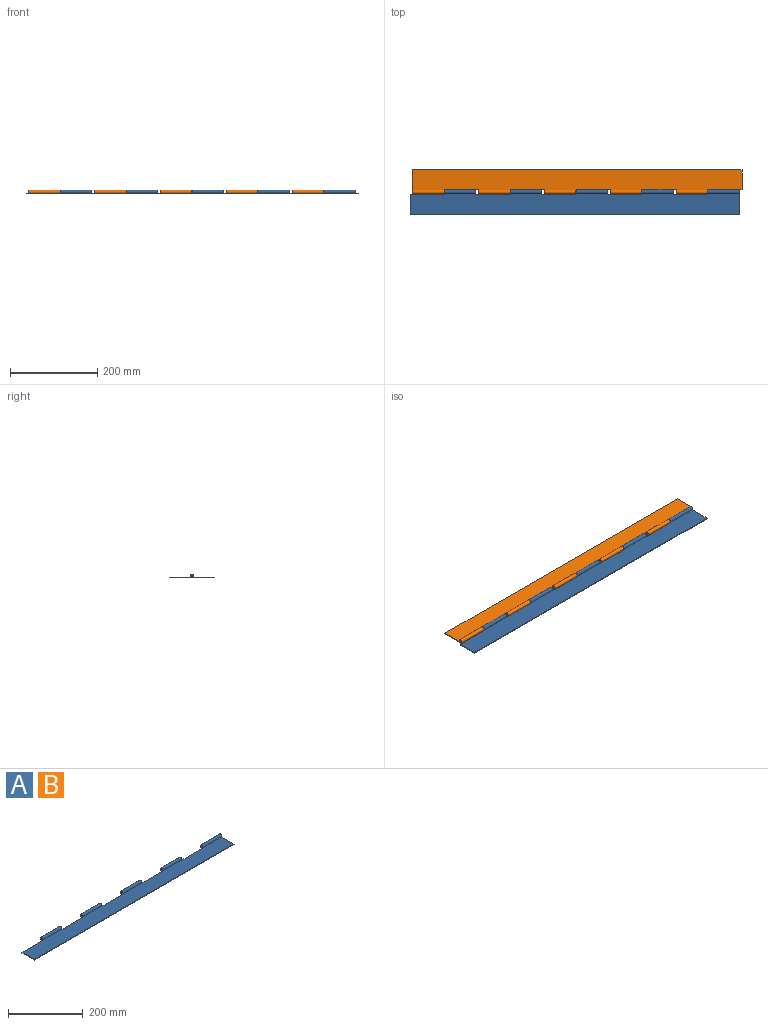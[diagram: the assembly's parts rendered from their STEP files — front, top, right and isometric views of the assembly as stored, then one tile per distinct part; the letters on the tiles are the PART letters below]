
ASSEMBLY  parts=2 mates=1
PART A: 29 faces, bbox 755.7x55.2x8.9 mm
  f0: cylinder r=4.45mm len=72.39mm, axis (-1,0,0), area 1712.7mm2, adj f11,f13,f14,f28
  f1: cylinder r=2.46mm len=72.39mm, axis (-1,0,0), area 1117.3mm2, adj f11,f28
  f2: cylinder r=4.45mm len=72.39mm, axis (-1,0,0), area 1712.7mm2, adj f13,f14,f25,f26
  f3: cylinder r=2.46mm len=72.39mm, axis (-1,0,0), area 1117.3mm2, adj f25,f26
  f4: cylinder r=4.45mm len=72.39mm, axis (-1,0,0), area 1712.7mm2, adj f13,f14,f22,f23
  f5: cylinder r=2.46mm len=72.39mm, axis (-1,0,0), area 1117.3mm2, adj f22,f23
  f6: cylinder r=4.45mm len=72.39mm, axis (-1,0,0), area 1712.7mm2, adj f13,f14,f19,f20
  f7: cylinder r=2.46mm len=72.39mm, axis (-1,0,0), area 1117.3mm2, adj f19,f20
  f8: plane 45.87x1.9mm, normal (-1,0,0), area 87mm2, adj f12,f13,f14,f15
  f9: cylinder r=4.45mm len=72.39mm, axis (-1,0,0), area 1712.7mm2, adj f13,f14,f16,f17
  f10: cylinder r=2.46mm len=72.39mm, axis (-1,0,0), area 1117.3mm2, adj f16,f17
  f11: plane 55.25x8.89mm, normal (1,0,0), area 134.7mm2, adj f0,f1,f12,f13,f14
  f12: plane 755.65x1.9mm, normal (0,-1,0), area 1433.8mm2, adj f8,f11,f13,f14
  f13: plane 755.65x50.8mm, normal (0,0,-1), area 36447.9mm2, adj f0,f2,f4,f6,f8,f9,f11,f12
  f14: plane 755.65x47.16mm, normal (0,0,1), area 35129.5mm2, adj f0,f2,f4,f6,f8,f9,f11,f12
  f15: plane 78.74x1.9mm, normal (0,1,0), area 149.4mm2, adj f8,f13,f14,f16
  f16: plane 9.37x8.89mm, normal (-1,0,0), area 47.6mm2, adj f9,f10,f13,f14,f15
  f17: plane 9.37x8.89mm, normal (1,0,0), area 47.6mm2, adj f9,f10,f13,f14,f18
  f18: plane 78.74x1.9mm, normal (0,1,0), area 149.4mm2, adj f13,f14,f17,f19
  f19: plane 9.37x8.89mm, normal (-1,0,0), area 47.6mm2, adj f6,f7,f13,f14,f18
  f20: plane 9.37x8.89mm, normal (1,0,0), area 47.6mm2, adj f6,f7,f13,f14,f21
  f21: plane 78.74x1.9mm, normal (0,1,0), area 149.4mm2, adj f13,f14,f20,f22
  f22: plane 9.37x8.89mm, normal (-1,0,0), area 47.6mm2, adj f4,f5,f13,f14,f21
  f23: plane 9.37x8.89mm, normal (1,0,0), area 47.6mm2, adj f4,f5,f13,f14,f24
  f24: plane 78.74x1.9mm, normal (0,1,0), area 149.4mm2, adj f13,f14,f23,f25
  f25: plane 9.37x8.89mm, normal (-1,0,0), area 47.6mm2, adj f2,f3,f13,f14,f24
  f26: plane 9.37x8.89mm, normal (1,0,0), area 47.6mm2, adj f2,f3,f13,f14,f27
  f27: plane 78.74x1.9mm, normal (0,1,0), area 149.4mm2, adj f13,f14,f26,f28
  f28: plane 9.37x8.89mm, normal (-1,0,0), area 47.6mm2, adj f0,f1,f13,f14,f27
PART B: same geometry as A
PLACE A t=(8.44,-41.06,36.81)mm fixed
PLACE B rot(axis=(0,0,-1),180deg) t=(14.79,9.75,36.92)mm
MATE cylindrical B.f0 <-> A.f0  axis (1,0,0) through (-290.65,-15.66,39.36)mm
